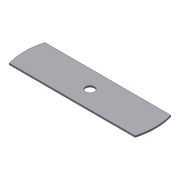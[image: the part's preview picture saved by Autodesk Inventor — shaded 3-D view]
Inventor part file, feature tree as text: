
AUTODESK INVENTOR PART (.ipt)
format: ipt  version: 2012 (Build 160160000, 160)  size: 72,192 bytes
history: native  units: in
note: dims shown in document units (in); Inventor stores cm internally (conversion verified against a paired STEP export)
features: extrude x1, sketch x1
ambient origin geometry x8: Origin, YZ Plane, XZ Plane, XY Plane, X Axis, Y Axis, Z Axis, Center Point
bodies: Solid1 (feature_tree)
feature tree (2):
  extrude  "Extrusion1"  Depth=5.5in
  sketch  "Sketch2"  dims[d0=3.0in d1=5.5in d2=0.625in d3=0.125in d4=0.0in]
